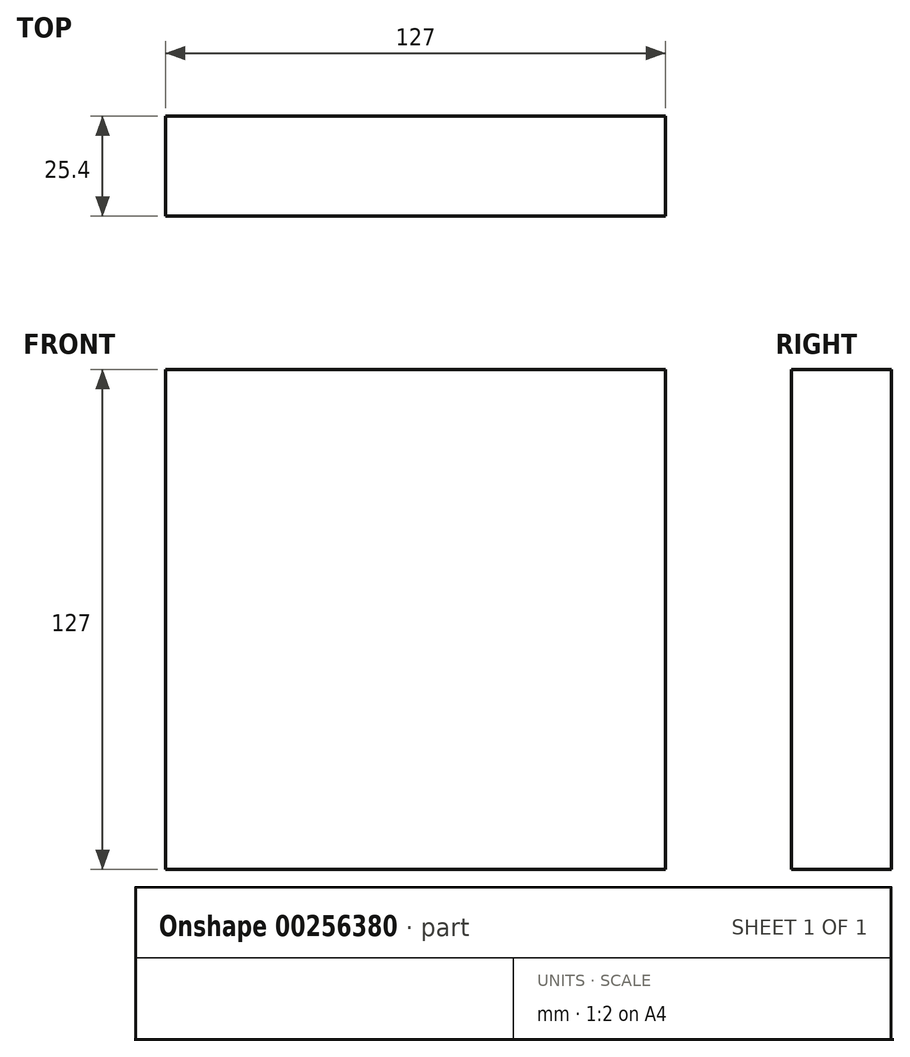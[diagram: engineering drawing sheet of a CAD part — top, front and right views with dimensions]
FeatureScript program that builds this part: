
annotation { "Feature Type Name" : "Feature", "Feature Type Description" : "" }
export const myFeature = defineFeature(function(context is Context, id is Id, definition is map)
    precondition{}
    {
        {
            var Q0;
            Q0=qCreatedBy(makeId("Front.planeOp"),FACE);
            var sketch = newSketch(context, id + "F0", { "sketchPlane" : qUnion([Q0])});
            skLineSegment(sketch, "E0.bottom", {"start": v(-58.07, 63.96) * mm, "end": v(68.93, 63.96) * mm});
            skLineSegment(sketch, "E0.top", {"start": v(-58.07, -63.04) * mm, "end": v(68.93, -63.04) * mm});
            skLineSegment(sketch, "E0.left", {"start": v(-58.07, 63.96) * mm, "end": v(-58.07, -63.04) * mm});
            skLineSegment(sketch, "E0.right", {"start": v(68.93, 63.96) * mm, "end": v(68.93, -63.04) * mm});
            skSolve(sketch);
        }
        {
            var Q0;
            Q0 = qSketchRegion(id + "F0", true);
            extrude(context, id + "F1", {"entities" : qUnion([Q0]), "depth" : 25.4 * mm});
        }
    });
